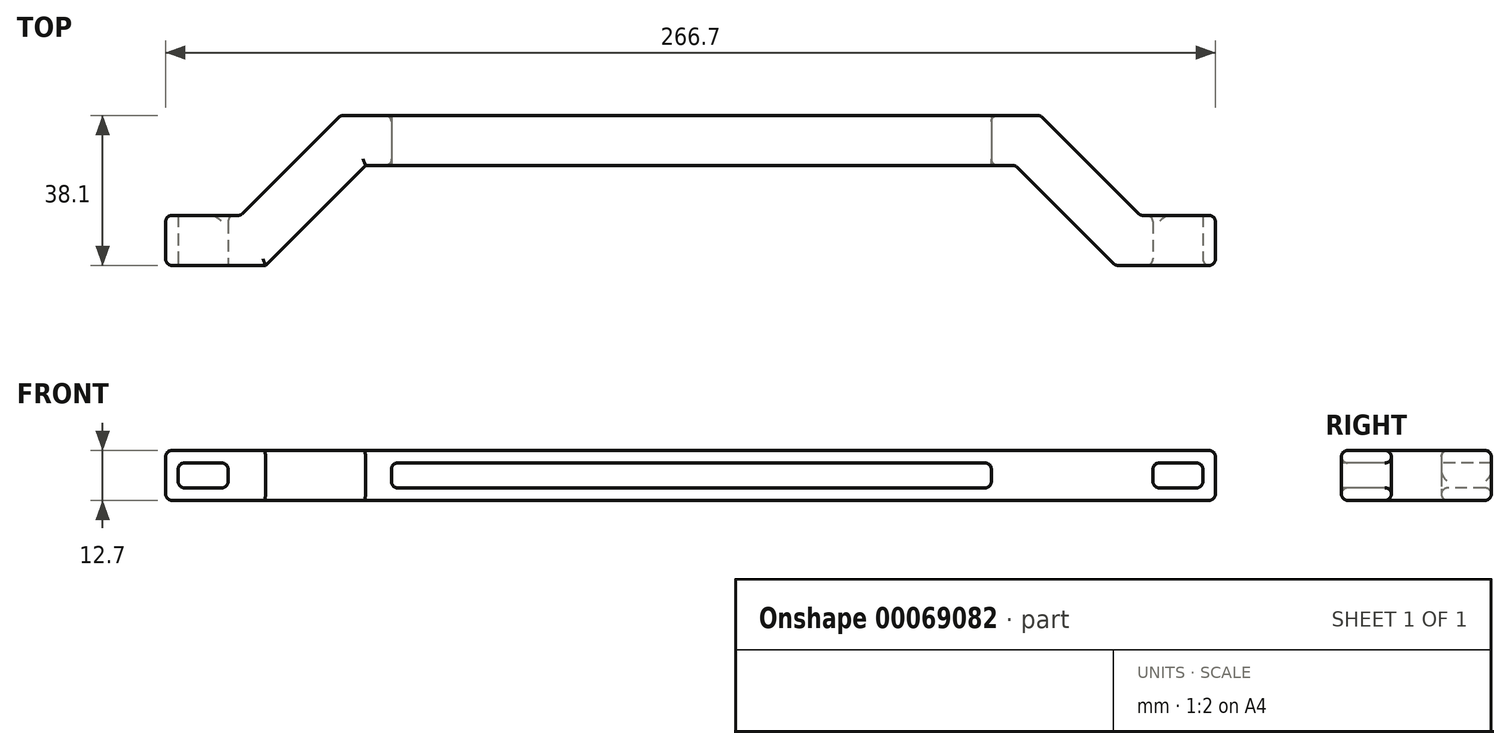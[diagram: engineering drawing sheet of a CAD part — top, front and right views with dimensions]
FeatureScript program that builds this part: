
annotation { "Feature Type Name" : "Feature", "Feature Type Description" : "" }
export const myFeature = defineFeature(function(context is Context, id is Id, definition is map)
    precondition{}
    {
        {
            var Q0;
            Q0=qCreatedBy(makeId("Top.planeOp"),FACE);
            var sketch = newSketch(context, id + "F0", { "sketchPlane" : qUnion([Q0])});
            skLineSegment(sketch, "E0", {"start": v(-82.3, 45.16) * mm, "end": v(95.5, 45.16) * mm});
            skLineSegment(sketch, "E1", {"start": v(95.5, 45.16) * mm, "end": v(120.9, 19.76) * mm});
            skLineSegment(sketch, "E2", {"start": v(120.9, 19.76) * mm, "end": v(139.95, 19.76) * mm});
            skLineSegment(sketch, "E3", {"start": v(139.95, 19.76) * mm, "end": v(139.95, 7.06) * mm});
            skLineSegment(sketch, "E4", {"start": v(139.95, 7.06) * mm, "end": v(114.55, 7.06) * mm});
            skLineSegment(sketch, "E5", {"start": v(114.55, 7.06) * mm, "end": v(89.15, 32.46) * mm});
            skLineSegment(sketch, "E6", {"start": v(89.15, 32.46) * mm, "end": v(-75.95, 32.46) * mm});
            skLineSegment(sketch, "E7", {"start": v(-75.95, 32.46) * mm, "end": v(-101.35, 7.06) * mm});
            skLineSegment(sketch, "E8", {"start": v(-101.35, 7.06) * mm, "end": v(-126.75, 7.06) * mm});
            skLineSegment(sketch, "E9", {"start": v(-126.75, 7.06) * mm, "end": v(-126.75, 19.76) * mm});
            skLineSegment(sketch, "E10", {"start": v(-126.75, 19.76) * mm, "end": v(-107.7, 19.76) * mm});
            skLineSegment(sketch, "E11", {"start": v(-107.7, 19.76) * mm, "end": v(-82.3, 45.16) * mm});
            skSolve(sketch);
        }
        {
            var Q0;
            Q0=makeQuery(id+"F0.imprint","IMPRINT",FACE,{"disambiguationData":[TD([[makeQuery(id+"F0.imprint","IMPRINT",EDGE,{"derivedFrom":sQuery(id+"F0.wireOp",EDGE,"E0")}),-1.0]])]});
            extrude(context, id + "F1", {"entities" : qUnion([Q0]), "depth" : 12.7 * mm});
        }
        {
            var Q0;
            Q0=qCreatedBy(makeId("Front.planeOp"),FACE);
            var sketch = newSketch(context, id + "F2", { "sketchPlane" : qUnion([Q0])});
            skLineSegment(sketch, "E12.bottom", {"start": v(-69.39, 9.53) * mm, "end": v(83.01, 9.53) * mm});
            skLineSegment(sketch, "E12.top", {"start": v(-69.39, 3.17) * mm, "end": v(83.01, 3.17) * mm});
            skLineSegment(sketch, "E12.left", {"start": v(-69.39, 9.53) * mm, "end": v(-69.39, 3.17) * mm});
            skLineSegment(sketch, "E12.right", {"start": v(83.01, 9.52) * mm, "end": v(83.01, 3.17) * mm});
            skSolve(sketch);
        }
        {
            var Q0;
            Q0 = qSketchRegion(id + "F2", true);
            extrude(context, id + "F3", {"entities" : qUnion([Q0]), "operationType" : NewBodyOperationType.REMOVE, "endBound" : BoundingType.THROUGH_ALL, "oppositeDirection" : true, "depth" : 25.4 * mm});
        }
        {
            var Q0;
            Q0=makeQuery(id+"F3.boolean.opBoolean","COPY",EDGE,{"derivedFrom":makeQuery(id+"F3.opExtrude","SWEPT_EDGE",EDGE,{"disambiguationData":[OSD([sQuery(id+"F2.wireOp",EDGE,"E12.top"),sQuery(id+"F2.wireOp",EDGE,"E12.left")])]})});
            var Q1;
            Q1=makeQuery(id+"F3.boolean.opBoolean","COPY",EDGE,{"derivedFrom":makeQuery(id+"F3.opExtrude","SWEPT_EDGE",EDGE,{"disambiguationData":[OSD([sQuery(id+"F2.wireOp",EDGE,"E12.bottom"),sQuery(id+"F2.wireOp",EDGE,"E12.left")])]})});
            var Q2;
            Q2=makeQuery(id+"F3.boolean.opBoolean","COPY",EDGE,{"derivedFrom":makeQuery(id+"F3.opExtrude","SWEPT_EDGE",EDGE,{"disambiguationData":[OSD([sQuery(id+"F2.wireOp",EDGE,"E12.top"),sQuery(id+"F2.wireOp",EDGE,"E12.right")])]})});
            var Q3;
            Q3=makeQuery(id+"F3.boolean.opBoolean","COPY",EDGE,{"derivedFrom":makeQuery(id+"F3.opExtrude","SWEPT_EDGE",EDGE,{"disambiguationData":[OSD([sQuery(id+"F2.wireOp",EDGE,"E12.bottom"),sQuery(id+"F2.wireOp",EDGE,"E12.right")])]})});
            var Q4;
            Q4=makeQuery(id+"F3.boolean.opBoolean","INTERSECT",EDGE,{"derivedFrom":[makeQuery(id+"F1.opExtrude","SWEPT_FACE",FACE,{"disambiguationData":[OSD([sQuery(id+"F0.wireOp",EDGE,"E6")])]}),makeQuery(id+"F3.opExtrude","SWEPT_FACE",FACE,{"disambiguationData":[OSD([sQuery(id+"F2.wireOp",EDGE,"E12.top")])]})]});
            var Q5;
            Q5=makeQuery(id+"F3.boolean.opBoolean","INTERSECT",EDGE,{"derivedFrom":[makeQuery(id+"F1.opExtrude","SWEPT_FACE",FACE,{"disambiguationData":[OSD([sQuery(id+"F0.wireOp",EDGE,"E0")])]}),makeQuery(id+"F3.opExtrude","SWEPT_FACE",FACE,{"disambiguationData":[OSD([sQuery(id+"F2.wireOp",EDGE,"E12.top")])]})]});
            fillet(context, id + "F4", {"entities" : qUnion([Q0, Q1, Q2, Q3, Q4, Q5]), "radius" : 1.59 * mm, "tangentPropagation" : true, "allowEdgeOverflow" : false});
        }
        {
            var Q0;
            Q0=makeQuery(id+"F1.opExtrude","SWEPT_FACE",FACE,{"disambiguationData":[OSD([sQuery(id+"F0.wireOp",EDGE,"E8")])]});
            var sketch = newSketch(context, id + "F5", { "sketchPlane" : qUnion([Q0])});
            skLineSegment(sketch, "E13.bottom", {"start": v(-123.58, 9.52) * mm, "end": v(-110.88, 9.52) * mm});
            skLineSegment(sketch, "E13.top", {"start": v(-123.58, 3.17) * mm, "end": v(-110.88, 3.17) * mm});
            skLineSegment(sketch, "E13.left", {"start": v(-123.58, 9.52) * mm, "end": v(-123.58, 3.17) * mm});
            skLineSegment(sketch, "E13.right", {"start": v(-110.88, 9.52) * mm, "end": v(-110.88, 3.17) * mm});
            skLineSegment(sketch, "E14.bottom", {"start": v(124.07, 9.52) * mm, "end": v(136.77, 9.52) * mm});
            skLineSegment(sketch, "E14.top", {"start": v(124.07, 3.17) * mm, "end": v(136.77, 3.17) * mm});
            skLineSegment(sketch, "E14.left", {"start": v(124.07, 9.52) * mm, "end": v(124.07, 3.17) * mm});
            skLineSegment(sketch, "E14.right", {"start": v(136.77, 9.52) * mm, "end": v(136.77, 3.17) * mm});
            skSolve(sketch);
        }
        {
            var Q0;
            Q0 = qSketchRegion(id + "F5", true);
            extrude(context, id + "F6", {"entities" : qUnion([Q0]), "operationType" : NewBodyOperationType.REMOVE, "endBound" : BoundingType.THROUGH_ALL, "oppositeDirection" : true, "depth" : 25.4 * mm});
        }
        {
            var Q0;
            Q0=makeQuery(id+"F6.boolean.opBoolean","COPY",EDGE,{"derivedFrom":makeQuery(id+"F6.opExtrude","SWEPT_EDGE",EDGE,{"disambiguationData":[OSD([sQuery(id+"F5.wireOp",EDGE,"E13.bottom"),sQuery(id+"F5.wireOp",EDGE,"E13.left")])]})});
            var Q1;
            Q1=makeQuery(id+"F6.boolean.opBoolean","COPY",EDGE,{"derivedFrom":makeQuery(id+"F6.opExtrude","SWEPT_EDGE",EDGE,{"disambiguationData":[OSD([sQuery(id+"F5.wireOp",EDGE,"E13.top"),sQuery(id+"F5.wireOp",EDGE,"E13.left")])]})});
            var Q2;
            Q2=makeQuery(id+"F6.boolean.opBoolean","COPY",EDGE,{"derivedFrom":makeQuery(id+"F6.opExtrude","SWEPT_EDGE",EDGE,{"disambiguationData":[OSD([sQuery(id+"F5.wireOp",EDGE,"E13.top"),sQuery(id+"F5.wireOp",EDGE,"E13.right")])]})});
            var Q3;
            Q3=makeQuery(id+"F6.boolean.opBoolean","COPY",EDGE,{"derivedFrom":makeQuery(id+"F6.opExtrude","SWEPT_EDGE",EDGE,{"disambiguationData":[OSD([sQuery(id+"F5.wireOp",EDGE,"E13.bottom"),sQuery(id+"F5.wireOp",EDGE,"E13.right")])]})});
            var Q4;
            Q4=makeQuery(id+"F6.boolean.opBoolean","COPY",EDGE,{"derivedFrom":makeQuery(id+"F6.opExtrude","CAP_EDGE",EDGE,{"disambiguationData":[OSD([sQuery(id+"F5.wireOp",EDGE,"E13.top")])],"isStart":true})});
            var Q5;
            Q5=makeQuery(id+"F6.boolean.opBoolean","COPY",EDGE,{"derivedFrom":makeQuery(id+"F6.opExtrude","SWEPT_EDGE",EDGE,{"disambiguationData":[OSD([sQuery(id+"F5.wireOp",EDGE,"E14.top"),sQuery(id+"F5.wireOp",EDGE,"E14.left")])]})});
            var Q6;
            Q6=makeQuery(id+"F6.boolean.opBoolean","COPY",EDGE,{"derivedFrom":makeQuery(id+"F6.opExtrude","SWEPT_EDGE",EDGE,{"disambiguationData":[OSD([sQuery(id+"F5.wireOp",EDGE,"E14.bottom"),sQuery(id+"F5.wireOp",EDGE,"E14.left")])]})});
            var Q7;
            Q7=makeQuery(id+"F6.boolean.opBoolean","COPY",EDGE,{"derivedFrom":makeQuery(id+"F6.opExtrude","SWEPT_EDGE",EDGE,{"disambiguationData":[OSD([sQuery(id+"F5.wireOp",EDGE,"E14.bottom"),sQuery(id+"F5.wireOp",EDGE,"E14.right")])]})});
            var Q8;
            Q8=makeQuery(id+"F6.boolean.opBoolean","COPY",EDGE,{"derivedFrom":makeQuery(id+"F6.opExtrude","SWEPT_EDGE",EDGE,{"disambiguationData":[OSD([sQuery(id+"F5.wireOp",EDGE,"E14.top"),sQuery(id+"F5.wireOp",EDGE,"E14.right")])]})});
            var Q9;
            Q9=makeQuery(id+"F6.boolean.opBoolean","COPY",EDGE,{"derivedFrom":makeQuery(id+"F6.opExtrude","CAP_EDGE",EDGE,{"disambiguationData":[OSD([sQuery(id+"F5.wireOp",EDGE,"E14.top")])],"isStart":true})});
            var Q10;
            Q10=makeQuery(id+"F6.boolean.opBoolean","INTERSECT",EDGE,{"derivedFrom":[makeQuery(id+"F1.opExtrude","SWEPT_FACE",FACE,{"disambiguationData":[OSD([sQuery(id+"F0.wireOp",EDGE,"E10")])]}),makeQuery(id+"F6.opExtrude","SWEPT_FACE",FACE,{"disambiguationData":[OSD([sQuery(id+"F5.wireOp",EDGE,"E13.right")])]})]});
            var Q11;
            Q11=makeQuery(id+"F6.boolean.opBoolean","INTERSECT",EDGE,{"derivedFrom":[makeQuery(id+"F1.opExtrude","SWEPT_FACE",FACE,{"disambiguationData":[OSD([sQuery(id+"F0.wireOp",EDGE,"E2")])]}),makeQuery(id+"F6.opExtrude","SWEPT_FACE",FACE,{"disambiguationData":[OSD([sQuery(id+"F5.wireOp",EDGE,"E14.left")])]})]});
            fillet(context, id + "F7", {"entities" : qUnion([Q0, Q1, Q2, Q3, Q4, Q5, Q6, Q7, Q8, Q9, Q10, Q11]), "radius" : 1.59 * mm, "tangentPropagation" : true, "allowEdgeOverflow" : false});
        }
        {
            var Q0;
            Q0=makeQuery(id+"F1.opExtrude","CAP_EDGE",EDGE,{"disambiguationData":[OSD([sQuery(id+"F0.wireOp",EDGE,"E0")])],"isStart":false});
            var Q1;
            Q1=makeQuery(id+"F1.opExtrude","CAP_EDGE",EDGE,{"disambiguationData":[OSD([sQuery(id+"F0.wireOp",EDGE,"E0")])],"isStart":true});
            var Q2;
            Q2=makeQuery(id+"F1.opExtrude","CAP_EDGE",EDGE,{"disambiguationData":[OSD([sQuery(id+"F0.wireOp",EDGE,"E11")])],"isStart":false});
            var Q3;
            Q3=makeQuery(id+"F1.opExtrude","SWEPT_FACE",FACE,{"disambiguationData":[OSD([sQuery(id+"F0.wireOp",EDGE,"E11")])]});
            var Q4;
            Q4=makeQuery(id+"F1.opExtrude","SWEPT_FACE",FACE,{"disambiguationData":[OSD([sQuery(id+"F0.wireOp",EDGE,"E1")])]});
            var Q5;
            Q5=makeQuery(id+"F1.opExtrude","CAP_FACE",FACE,{"disambiguationData":[OSD([sQuery(id+"F0.wireOp",EDGE,"E0"),sQuery(id+"F0.wireOp",EDGE,"E1"),sQuery(id+"F0.wireOp",EDGE,"E2"),sQuery(id+"F0.wireOp",EDGE,"E3"),sQuery(id+"F0.wireOp",EDGE,"E4"),sQuery(id+"F0.wireOp",EDGE,"E5"),sQuery(id+"F0.wireOp",EDGE,"E6"),sQuery(id+"F0.wireOp",EDGE,"E7"),sQuery(id+"F0.wireOp",EDGE,"E8"),sQuery(id+"F0.wireOp",EDGE,"E9"),sQuery(id+"F0.wireOp",EDGE,"E10"),sQuery(id+"F0.wireOp",EDGE,"E11")])],"isStart":false});
            var Q6;
            Q6=makeQuery(id+"F1.opExtrude","CAP_FACE",FACE,{"disambiguationData":[OSD([sQuery(id+"F0.wireOp",EDGE,"E0"),sQuery(id+"F0.wireOp",EDGE,"E1"),sQuery(id+"F0.wireOp",EDGE,"E2"),sQuery(id+"F0.wireOp",EDGE,"E3"),sQuery(id+"F0.wireOp",EDGE,"E4"),sQuery(id+"F0.wireOp",EDGE,"E5"),sQuery(id+"F0.wireOp",EDGE,"E6"),sQuery(id+"F0.wireOp",EDGE,"E7"),sQuery(id+"F0.wireOp",EDGE,"E8"),sQuery(id+"F0.wireOp",EDGE,"E9"),sQuery(id+"F0.wireOp",EDGE,"E10"),sQuery(id+"F0.wireOp",EDGE,"E11")])],"isStart":true});
            var Q7;
            Q7=makeQuery(id+"F1.opExtrude","SWEPT_FACE",FACE,{"disambiguationData":[OSD([sQuery(id+"F0.wireOp",EDGE,"E4")])]});
            var Q8;
            Q8=makeQuery(id+"F1.opExtrude","SWEPT_FACE",FACE,{"disambiguationData":[OSD([sQuery(id+"F0.wireOp",EDGE,"E5")])]});
            var Q9;
            Q9=makeQuery(id+"F1.opExtrude","SWEPT_FACE",FACE,{"disambiguationData":[OSD([sQuery(id+"F0.wireOp",EDGE,"E9")])]});
            fillet(context, id + "F8", {"entities" : qUnion([Q0, Q1, Q2, Q3, Q4, Q5, Q6, Q7, Q8, Q9]), "radius" : 1.59 * mm, "tangentPropagation" : true, "allowEdgeOverflow" : false});
        }
        {
            var Q0;
            Q0=makeQuery(id+"F1.opExtrude","SWEPT_FACE",FACE,{"disambiguationData":[OSD([sQuery(id+"F0.wireOp",EDGE,"E3")])]});
            fillet(context, id + "F9", {"entities" : qUnion([Q0]), "radius" : 1.59 * mm, "tangentPropagation" : true, "allowEdgeOverflow" : false});
        }
    });
